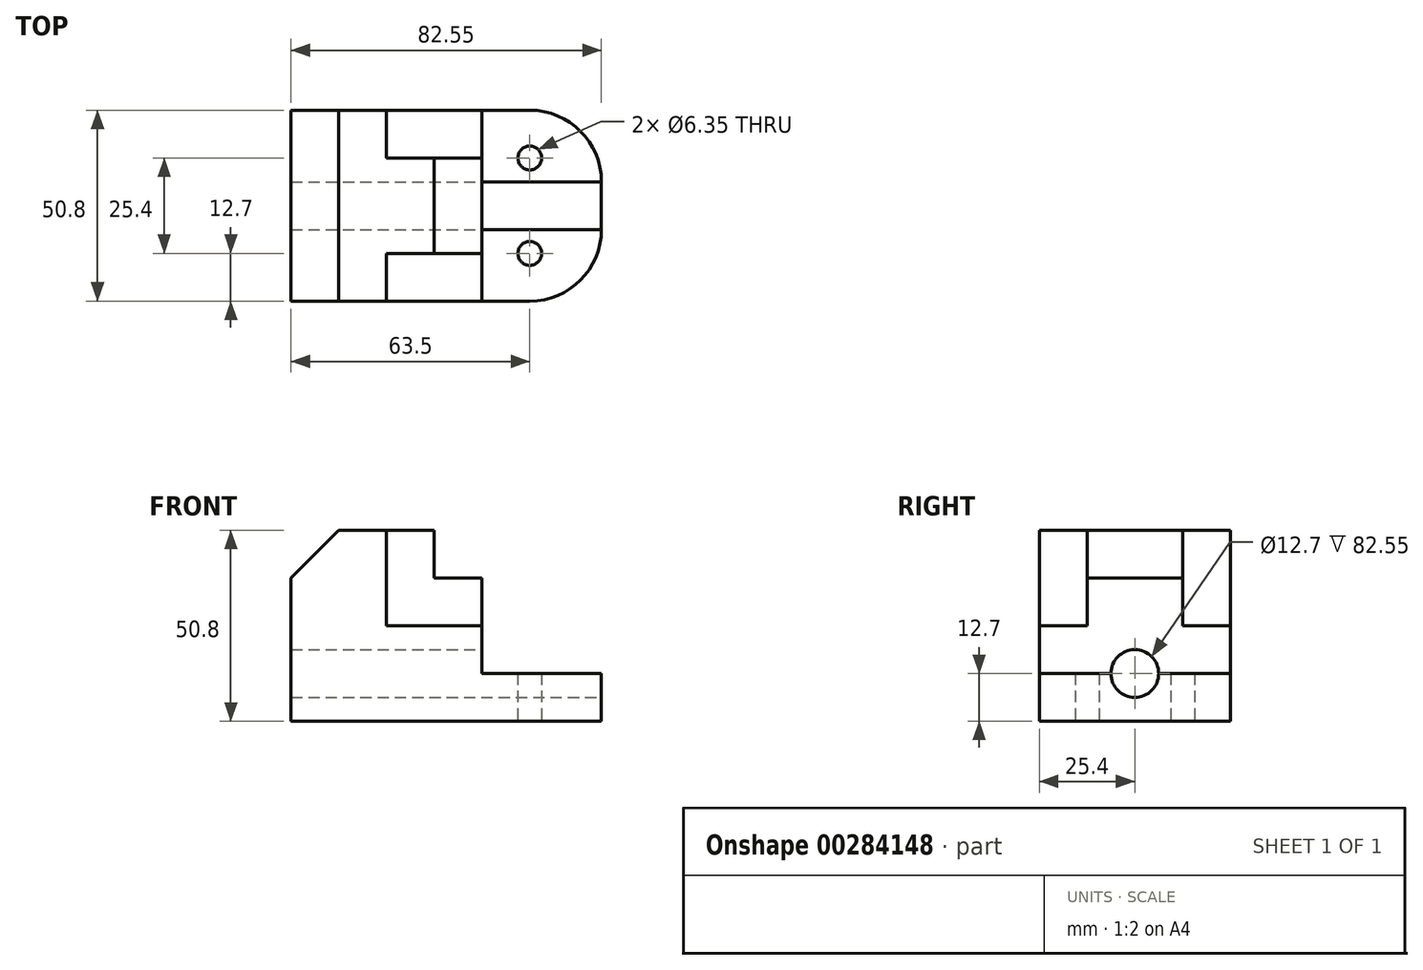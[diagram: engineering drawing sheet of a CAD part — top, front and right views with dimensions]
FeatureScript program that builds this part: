
annotation { "Feature Type Name" : "Feature", "Feature Type Description" : "" }
export const myFeature = defineFeature(function(context is Context, id is Id, definition is map)
    precondition{}
    {
        {
            var Q0;
            Q0=qCreatedBy(makeId("Top.planeOp"),FACE);
            var sketch = newSketch(context, id + "F0", { "sketchPlane" : qUnion([Q0])});
            skLineSegment(sketch, "E0", {"start": v(-38.1, 25.4) * mm, "end": v(-38.1, -25.4) * mm});
            skLineSegment(sketch, "E1", {"start": v(-12.7, -25.4) * mm, "end": v(-12.7, -12.7) * mm});
            skLineSegment(sketch, "E2", {"start": v(-12.7, -12.7) * mm, "end": v(12.7, -12.7) * mm});
            skLineSegment(sketch, "E3", {"start": v(12.7, -12.7) * mm, "end": v(12.7, -25.4) * mm});
            skLineSegment(sketch, "E4", {"start": v(12.7, -25.4) * mm, "end": v(25.4, -25.4) * mm});
            skLineSegment(sketch, "E5", {"start": v(-38.1, -25.4) * mm, "end": v(-12.7, -25.4) * mm});
            skLineSegment(sketch, "E6", {"start": v(0, -12.7) * mm, "end": v(0, 12.7) * mm});
            skLineSegment(sketch, "E7", {"start": v(0, 12.7) * mm, "end": v(-12.7, 12.7) * mm});
            skLineSegment(sketch, "E8", {"start": v(-12.7, 12.7) * mm, "end": v(-12.7, 25.4) * mm});
            skLineSegment(sketch, "E9", {"start": v(-12.7, 25.4) * mm, "end": v(-38.1, 25.4) * mm});
            skLineSegment(sketch, "E10", {"start": v(0, 12.7) * mm, "end": v(12.7, 12.7) * mm});
            skLineSegment(sketch, "E11", {"start": v(12.7, 12.7) * mm, "end": v(12.7, 25.4) * mm});
            skLineSegment(sketch, "E12", {"start": v(12.7, 25.4) * mm, "end": v(25.4, 25.4) * mm});
            skLineSegment(sketch, "E13", {"start": v(12.7, 12.7) * mm, "end": v(12.7, 6.35) * mm});
            skLineSegment(sketch, "E14", {"start": v(12.7, 6.35) * mm, "end": v(44.45, 6.35) * mm});
            skLineSegment(sketch, "E15", {"start": v(44.45, 6.35) * mm, "end": v(44.45, -6.35) * mm});
            skLineSegment(sketch, "E16", {"start": v(44.45, -6.35) * mm, "end": v(12.7, -6.35) * mm});
            skLineSegment(sketch, "E17", {"start": v(12.7, -6.35) * mm, "end": v(12.7, -12.7) * mm});
            skLineSegment(sketch, "E18", {"start": v(12.7, 6.35) * mm, "end": v(12.7, -6.35) * mm});
            skArc(sketch, "E19", {"start": v(25.4, 25.4) * mm, "mid": v(38.87, 19.82) * mm, "end": v(44.45, 6.35) * mm});
            skArc(sketch, "E20", {"start": v(25.4, -25.4) * mm, "mid": v(38.87, -19.82) * mm, "end": v(44.45, -6.35) * mm});
            skLineSegment(sketch, "E21", {"start": v(-12.7, -25.4) * mm, "end": v(12.7, -25.4) * mm});
            skLineSegment(sketch, "E22", {"start": v(-12.7, 25.4) * mm, "end": v(12.7, 25.4) * mm});
            skLineSegment(sketch, "E23", {"start": v(-25.4, 25.4) * mm, "end": v(-25.4, -25.4) * mm});
            skCircle(sketch, "E24", {"center": v(25.4, 12.7) * mm, "radius": 3.18 * mm});
            skCircle(sketch, "E25", {"center": v(25.4, -12.7) * mm, "radius": 3.18 * mm});
            skSolve(sketch);
        }
        {
            var Q0;
            Q0=makeQuery(id+"F0.imprint","IMPRINT",FACE,{"disambiguationData":[TD([[makeQuery(id+"F0.imprint","IMPRINT",EDGE,{"derivedFrom":sQuery(id+"F0.wireOp",EDGE,"E3")}),1.0]])]});
            var Q1;
            Q1=makeQuery(id+"F0.imprint","IMPRINT",FACE,{"disambiguationData":[TD([[makeQuery(id+"F0.imprint","IMPRINT",EDGE,{"derivedFrom":sQuery(id+"F0.wireOp",EDGE,"E14")}),-1.0]])]});
            var Q2;
            Q2=makeQuery(id+"F0.imprint","IMPRINT",FACE,{"disambiguationData":[TD([[makeQuery(id+"F0.imprint","IMPRINT",EDGE,{"derivedFrom":sQuery(id+"F0.wireOp",EDGE,"E11")}),-1.0]])]});
            extrude(context, id + "F1", {"entities" : qUnion([Q0, Q1, Q2]), "depth" : 12.7 * mm});
        }
        {
            var Q0;
            {var subQ3=sQuery(id+"F0.wireOp",EDGE,"E1");Q0=makeQuery(id+"F0.imprint","IMPRINT",FACE,{"disambiguationData":[TD([[makeQuery(id+"F0.imprint","IMPRINT",EDGE,{"derivedFrom":subQ3}),-1.0]])]});}
            var Q1;
            Q1=makeQuery(id+"F0.imprint","IMPRINT",FACE,{"disambiguationData":[TD([[makeQuery(id+"F0.imprint","IMPRINT",EDGE,{"derivedFrom":sQuery(id+"F0.wireOp",EDGE,"E7")}),-1.0]])]});
            extrude(context, id + "F2", {"entities" : qUnion([Q0, Q1]), "operationType" : NewBodyOperationType.ADD, "depth" : 25.4 * mm});
        }
        {
            var Q0;
            {var subQ0=sQuery(id+"F0.wireOp",EDGE,"E6");Q0=makeQuery(id+"F0.imprint","IMPRINT",FACE,{"disambiguationData":[TD([[makeQuery(id+"F0.imprint","IMPRINT",EDGE,{"derivedFrom":subQ0}),-1.0]])]});}
            extrude(context, id + "F3", {"entities" : qUnion([Q0]), "operationType" : NewBodyOperationType.ADD, "depth" : 38.1 * mm});
        }
        {
            var Q0;
            {var subQ0=sQuery(id+"F0.wireOp",EDGE,"E0");Q0=makeQuery(id+"F0.imprint","IMPRINT",FACE,{"disambiguationData":[TD([[makeQuery(id+"F0.imprint","IMPRINT",EDGE,{"derivedFrom":subQ0}),1.0]])]});}
            var Q1;
            {var subQ2=sQuery(id+"F0.wireOp",EDGE,"E1");Q1=makeQuery(id+"F0.imprint","IMPRINT",FACE,{"disambiguationData":[TD([[makeQuery(id+"F0.imprint","IMPRINT",EDGE,{"derivedFrom":subQ2}),1.0]])]});}
            extrude(context, id + "F4", {"entities" : qUnion([Q0, Q1]), "operationType" : NewBodyOperationType.ADD, "depth" : 50.8 * mm});
        }
        {
            var Q0;
            Q0=makeQuery(id+"F4.boolean.opBoolean","MERGE",FACE,{"derivedFrom":[makeQuery(id+"F2.boolean.opBoolean","MERGE",FACE,{"derivedFrom":[makeQuery(id+"F1.opExtrude","SWEPT_FACE",FACE,{"disambiguationData":[OSD([sQuery(id+"F0.wireOp",EDGE,"E4")])]}),makeQuery(id+"F2.opExtrude","SWEPT_FACE",FACE,{"disambiguationData":[OSD([sQuery(id+"F0.wireOp",EDGE,"E21")])]})]}),makeQuery(id+"F4.opExtrude","SWEPT_FACE",FACE,{"disambiguationData":[OSD([sQuery(id+"F0.wireOp",EDGE,"E5")])]})]});
            var sketch = newSketch(context, id + "F5", { "sketchPlane" : qUnion([Q0])});
            skLineSegment(sketch, "E26", {"start": v(-38.1, 50.8) * mm, "end": v(-25.4, 50.8) * mm});
            skLineSegment(sketch, "E27", {"start": v(-25.4, 50.8) * mm, "end": v(-38.1, 38.1) * mm});
            skLineSegment(sketch, "E28", {"start": v(-38.1, 38.1) * mm, "end": v(-38.1, 50.8) * mm});
            skSolve(sketch);
        }
        {
            var Q0;
            Q0=makeQuery(id+"F5.imprint","IMPRINT",FACE,{"disambiguationData":[TD([[makeQuery(id+"F5.imprint","IMPRINT",EDGE,{"derivedFrom":sQuery(id+"F5.wireOp",EDGE,"E26")}),-1.0]])]});
            extrude(context, id + "F6", {"entities" : qUnion([Q0]), "operationType" : NewBodyOperationType.REMOVE, "endBound" : BoundingType.THROUGH_ALL, "oppositeDirection" : true, "depth" : 25.4 * mm});
        }
        {
            var Q0;
            Q0=makeQuery(id+"F1.opExtrude","SWEPT_FACE",FACE,{"disambiguationData":[OSD([sQuery(id+"F0.wireOp",EDGE,"E15")])]});
            var sketch = newSketch(context, id + "F7", { "sketchPlane" : qUnion([Q0])});
            skCircle(sketch, "E29", {"center": v(0, 12.7) * mm, "radius": 6.35 * mm});
            skSolve(sketch);
        }
        {
            var Q0;
            {var subQ1=sQuery(id+"F0.wireOp",EDGE,"E15");var subQ2=makeQuery(id+"F1.opExtrude","CAP_EDGE",EDGE,{"disambiguationData":[OSD([subQ1])],"isStart":false});Q0=makeQuery(id+"F7.imprint","IMPRINT",FACE,{"disambiguationData":[TD([[makeQuery(id+"F7.imprint","IMPRINT",EDGE,{"derivedFrom":subQ2}),-1.0]])]});}
            var Q1;
            {var subQ1=sQuery(id+"F0.wireOp",EDGE,"E15");var subQ2=makeQuery(id+"F1.opExtrude","CAP_EDGE",EDGE,{"disambiguationData":[OSD([subQ1])],"isStart":false});Q1=makeQuery(id+"F7.imprint","IMPRINT",FACE,{"disambiguationData":[TD([[makeQuery(id+"F7.imprint","IMPRINT",EDGE,{"derivedFrom":subQ2}),1.0]])]});}
            extrude(context, id + "F8", {"entities" : qUnion([Q0, Q1]), "operationType" : NewBodyOperationType.REMOVE, "endBound" : BoundingType.THROUGH_ALL, "oppositeDirection" : true, "depth" : 25.4 * mm});
        }
    });
